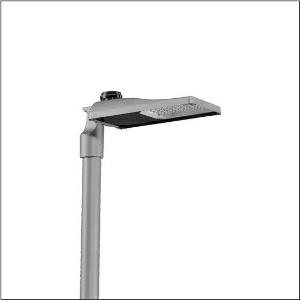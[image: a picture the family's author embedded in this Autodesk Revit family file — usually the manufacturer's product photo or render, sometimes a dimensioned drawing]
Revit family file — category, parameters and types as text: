
# Revit family: streetlight_sl_31_mini___st0_8a_5xh6c45n08ja_4560
name_source: partatom
category: Lighting Fixtures
units: mm (PartAtom-declared; Revit-internal decimal feet)

## family parameters
Cut with Voids When Loaded = No
Host = Face
Light Source = No
Part Type = Normal
Room Calculation Point = No
Round Connector Dimension = Use Diameter
Shared = No

## types (1)
- --- (1 x LED, 12590 lm, 81.1 W, 4000K)
    Apparent Load = 81 VA
    CIE Flux Codes = 41 75 97 100 100
    Color Rendering = 70
    Color Temperature = 4000K
    Default Elevation = 1800 mm
    Description = Streetlight SL 31 mini NEMA (7pin), Desk-Remote mast luminaire for post-top, side-entry; light control with lens of PMMA; light distribution: ST0.8a, direct asymmetric distribution, for standard-compliant lighting for roads and squares; LED: luminous flux: 12.590lm, light colour: 740, colour temperature: 4000K; luminous efficacy: 155,2lm/W; control: pre-setting: linear dimming characteristic, flexible luminous flux parameterisation, time-dependent luminous flux control, constant luminous flux control, intelligent temperature release in ECG and LED module, overheat protection; luminaire housing, of diecast aluminium, Siteco® metallic grey (DB 702S), corrosivity category C5 high according to DIN EN ISO 12944; cover of toughened safety glass, transparent, opened without tools; mast flange of diecast aluminium, Siteco® metallic grey (DB 702S), spigot size: 76/60mm, mast flange included unmounted; with cable H07RN-F 3x 1.5mm², cable length: 10,5m, connection cable pre-assembled; mains connection: 220..240V, AC, 50/60Hz; power consumption (at start of service life): 81,1W / (at end of service life): 88,3W / (with reduced operation 50%): 36,4W; protection rating (complete): IP66; insulation class (complete): insulation class I (protective earthing); impact resistance: IK10; certification: CE, ENEC, ENEC+, VDE, UKCA; permissible operating ambient temperature for outdoor applications: -40..+50°C; packaging unit: 1 piece

Light Distribution: ST0.8a
    Height = 76 mm
    Lamp = 1 x LED
    Lamp Light Flux = 12590 lm
    Lamp Power = 81.1 W
    Lamp count = 1
    Length = 547 mm
    Luminous efficacy = 155 lm/W
    Manufacturer = Siteco
    ModVariant = No
    Model = 5XH6C45N08JA
    Number of Poles = 1
    OnlyDefault = Yes
    Power Factor = 1
    Product Name = Streetlight SL 31 mini | ST0.8a
    Product group = mast luminaire | pylon top
    ProductGroupID = 6100
    Protection Class = Protection class I
    Protection Degree = IP 66
    RLX_Detail_Level = 1
    RLX_Emergency_Light_Flux = 0 lm
    RLX_Emergency_Type = 0
    RLX_Emergency_Type_DB = No
    RlxData = <blob elided: 40385 chars, md5=047dce07>
    Socket = socket
    Standby Power = 0 W
    System Light Flux = 12590 lm
    System Power = 81 W
    Type Comments = factory setting: luminous flux: 100 % | dim-lin: 254 | 860 mA
    Type Image = l_1300322.jpg
    URL = http://relux.com
    VarID = @adj_049500
    Voltage = 0 V
    Weight = 0.00 kg
    Width = 265 mm

## geometry (parser evidence)
native form markers: Blend x4, Sweep x9
no freeform markers — native parametric forms only
